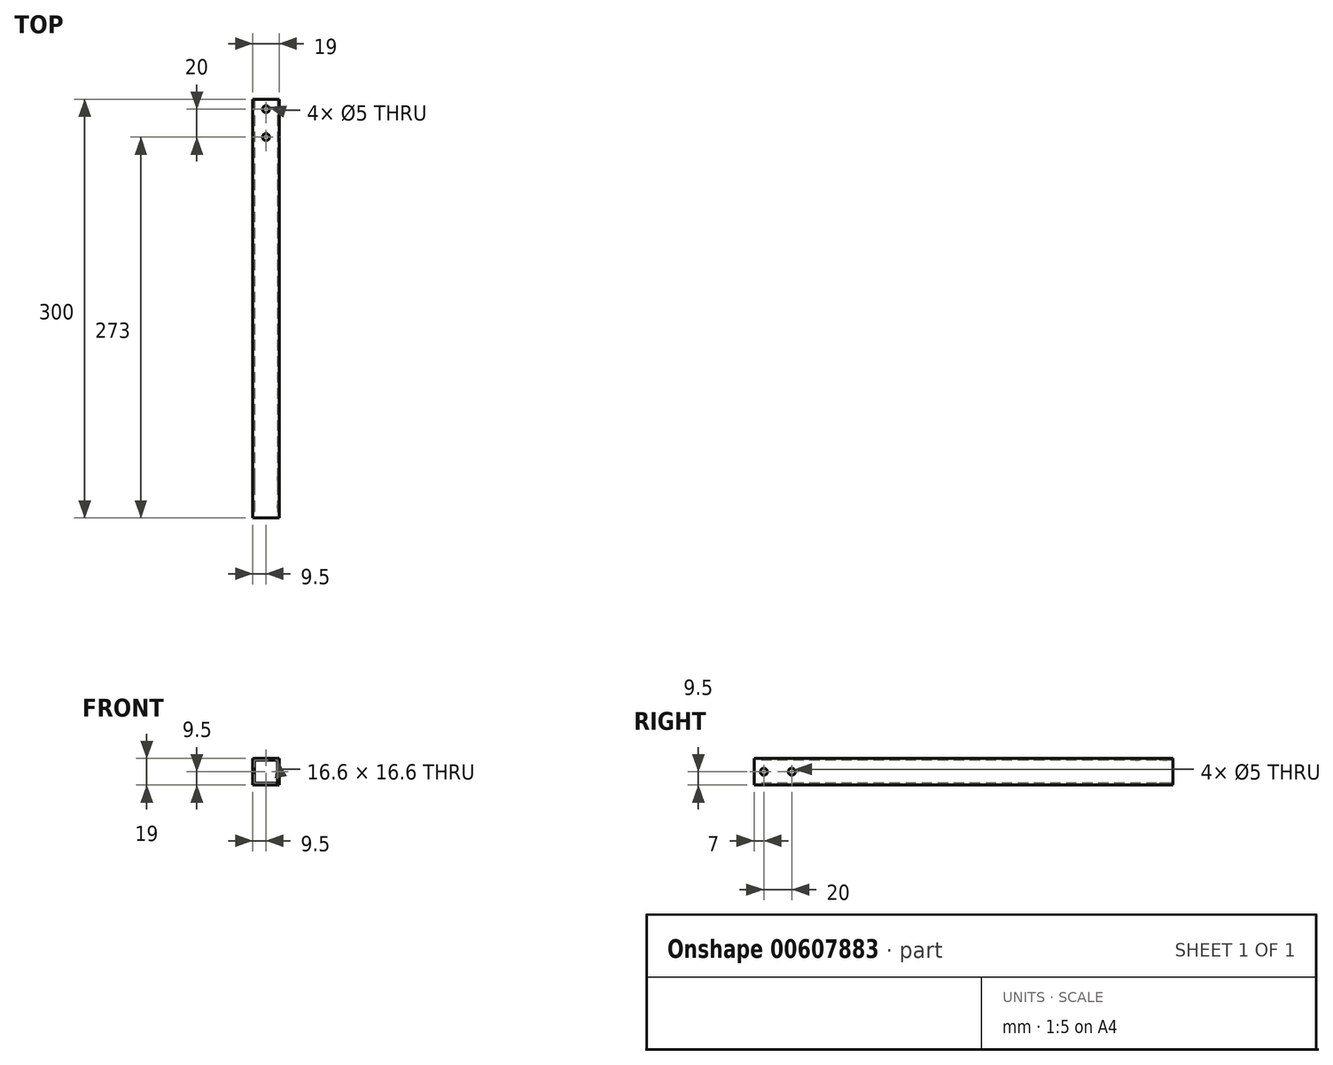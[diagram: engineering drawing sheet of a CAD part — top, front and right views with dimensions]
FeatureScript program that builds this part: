
annotation { "Feature Type Name" : "Feature", "Feature Type Description" : "" }
export const myFeature = defineFeature(function(context is Context, id is Id, definition is map)
    precondition{}
    {
        {
            assignVariable(context, id + "F0", {"name" : "Length", "anyValue" : 300});
        }
        {
            var Q0;
            Q0=qCreatedBy(makeId("Front.planeOp"),FACE);
            var sketch = newSketch(context, id + "F1", { "sketchPlane" : qUnion([Q0])});
            skLineSegment(sketch, "E0.bottom", {"start": v(-9.5, 9.5) * mm, "end": v(9.5, 9.5) * mm});
            skLineSegment(sketch, "E0.top", {"start": v(-9.5, -9.5) * mm, "end": v(9.5, -9.5) * mm});
            skLineSegment(sketch, "E0.left", {"start": v(-9.5, 9.5) * mm, "end": v(-9.5, -9.5) * mm});
            skLineSegment(sketch, "E0.right", {"start": v(9.5, 9.5) * mm, "end": v(9.5, -9.5) * mm});
            skLineSegment(sketch, "E1.bottom", {"start": v(-8.3, 8.3) * mm, "end": v(8.3, 8.3) * mm});
            skLineSegment(sketch, "E1.top", {"start": v(-8.3, -8.3) * mm, "end": v(8.3, -8.3) * mm});
            skLineSegment(sketch, "E1.left", {"start": v(-8.3, 8.3) * mm, "end": v(-8.3, -8.3) * mm});
            skLineSegment(sketch, "E1.right", {"start": v(8.3, 8.3) * mm, "end": v(8.3, -8.3) * mm});
            skSolve(sketch);
        }
        {
            var Q0;
            Q0=qSketchRegion(id+"F1",true);
            extrude(context, id + "F2", {"entities" : qUnion([Q0]), "oppositeDirection" : true, "depth" : (getVariable(context, 'Length')) * mm});
        }
        {
            var Q0;
            Q0=makeQuery(id+"F2.opExtrude","SWEPT_FACE",FACE,{"disambiguationData":[OSD([sQuery(id+"F1.wireOp",EDGE,"E0.right")])]});
            var sketch = newSketch(context, id + "F3", { "sketchPlane" : qUnion([Q0])});
            skPoint(sketch, "E2", {"position": v(27, 0) * mm});
            skPoint(sketch, "E3", {"position": v(7, 0) * mm});
            skPoint(sketch, "E4.positionSnap0", {"position": v(300, 0) * mm});
            skSolve(sketch);
        }
        {
            var Q0;
            Q0=makeQuery(id+"F2.opExtrude","SWEPT_FACE",FACE,{"disambiguationData":[OSD([sQuery(id+"F1.wireOp",EDGE,"E0.bottom")])]});
            var sketch = newSketch(context, id + "F4", { "sketchPlane" : qUnion([Q0])});
            skPoint(sketch, "E5", {"position": v(0, 273) * mm});
            skPoint(sketch, "E5.positionSnap0", {"position": v(0, 300) * mm});
            skPoint(sketch, "E6", {"position": v(0, 293) * mm});
            skSolve(sketch);
        }
        {
            var Q0;
            Q0=sQuery(id+"F3.wireOp",VERTEX,"E3");
            var Q1;
            Q1=sQuery(id+"F3.wireOp",VERTEX,"E2");
            var Q2;
            Q2=sQuery(id+"F3.wireOp",VERTEX,"E4");
            var Q3;
            Q3=sQuery(id+"F3.wireOp",VERTEX,"fbccbc36-4221-4630-8499-fa19f10c56a1");
            var Q4;
            Q4=sQuery(id+"F4.wireOp",VERTEX,"E5");
            var Q5;
            Q5=sQuery(id+"F4.wireOp",VERTEX,"E6");
            var Q6;
            Q6=makeQuery(id+"F2.opExtrude","SWEPT_BODY",BODY,{"disambiguationData":[OSD([sQuery(id+"F1.wireOp",EDGE,"E0.bottom"),sQuery(id+"F1.wireOp",EDGE,"E0.top"),sQuery(id+"F1.wireOp",EDGE,"E0.left"),sQuery(id+"F1.wireOp",EDGE,"E0.right"),sQuery(id+"F1.wireOp",EDGE,"E1.bottom"),sQuery(id+"F1.wireOp",EDGE,"E1.top"),sQuery(id+"F1.wireOp",EDGE,"E1.left"),sQuery(id+"F1.wireOp",EDGE,"E1.right")])]});
            hole(context, id + "F5", {"style" : HoleStyle.SIMPLE, "endStyle" : HoleEndStyle.THROUGH, "holeDiameter" : 5 * mm, "majorDiameter" : 5 * mm, "tappedDepth" : 12 * mm, "tapClearance" : 3, "locations" : qUnion([Q0, Q1, Q2, Q3, Q4, Q5]), "scope" : qUnion([Q6])});
        }
    });
